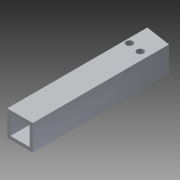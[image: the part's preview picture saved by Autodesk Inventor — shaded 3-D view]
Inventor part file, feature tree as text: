
AUTODESK INVENTOR PART (.ipt)
format: ipt  version: 2013 (Build 170138000, 138)  size: 97,792 bytes
history: native  units: in
note: dims shown in document units (in); Inventor stores cm internally (conversion verified against a paired STEP export)
features: extrude x3, sketch x3, reference x2
ambient origin geometry x8: Origin, YZ Plane, XZ Plane, XY Plane, X Axis, Y Axis, Z Axis, Center Point
bodies: Solid1 (feature_tree)
feature tree (8):
  extrude  "Extrusion1"  Depth=1.0in
  extrude  "Extrusion2"  Depth=5.5in TaperAngle=0.0deg
  extrude  "Extrusion3"  Depth=5.0in TaperAngle=0.0deg
  sketch  "Sketch1"  dims[d0=1.0in d1=1.0in]
  sketch  "Sketch2"  dims[d2=0.125in d3=5.5in d4=0.0in]
  sketch  "Sketch3"  dims[d5=0.0586in d6=5.0in d7=0.0in d8=2.5in d9=0.0in]
  reference  "Reference1"
  reference  "Reference2"
